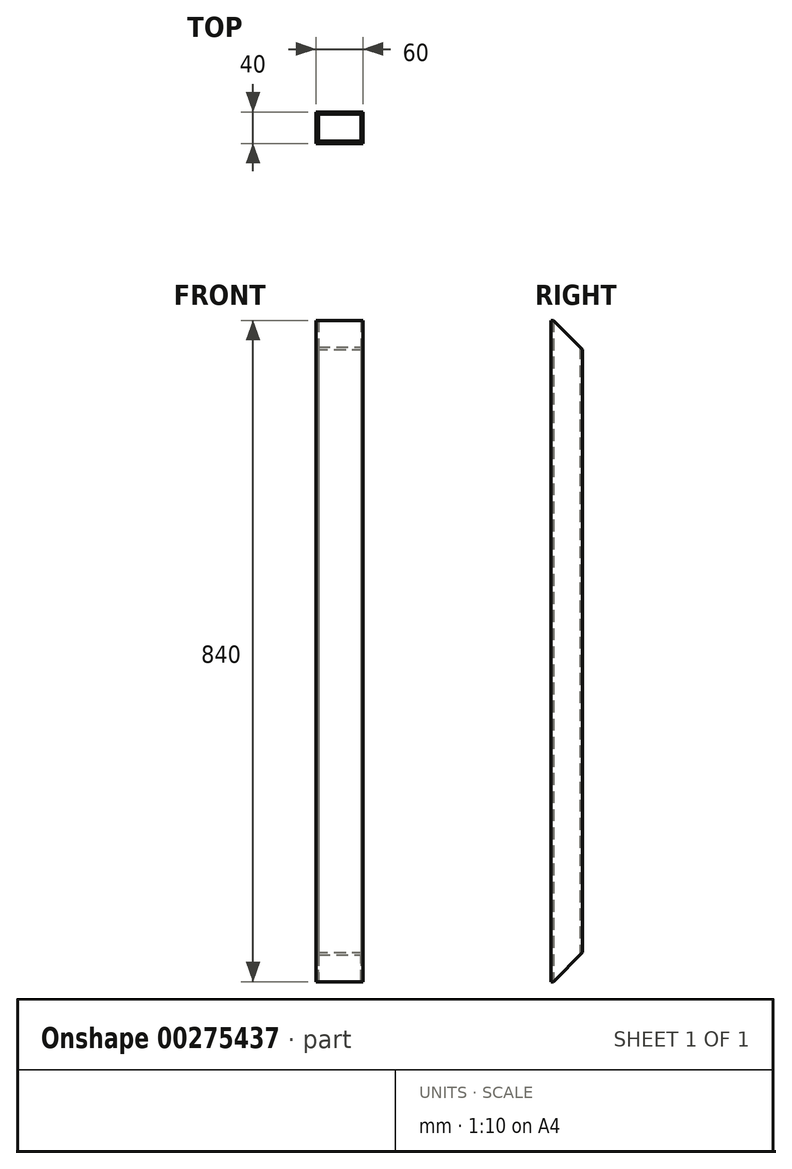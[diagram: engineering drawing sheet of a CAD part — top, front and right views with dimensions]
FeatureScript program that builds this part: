
annotation { "Feature Type Name" : "Feature", "Feature Type Description" : "" }
export const myFeature = defineFeature(function(context is Context, id is Id, definition is map)
    precondition{}
    {
        {
            var Q0;
            Q0=qCreatedBy(makeId("Top.planeOp"),FACE);
            var sketch = newSketch(context, id + "F0", { "sketchPlane" : qUnion([Q0])});
            skLineSegment(sketch, "E0.bottom", {"start": v(30, 20) * mm, "end": v(-30, 20) * mm});
            skLineSegment(sketch, "E0.top", {"start": v(30, -20) * mm, "end": v(-30, -20) * mm});
            skLineSegment(sketch, "E0.left", {"start": v(30, 20) * mm, "end": v(30, -20) * mm});
            skLineSegment(sketch, "E0.right", {"start": v(-30, 20) * mm, "end": v(-30, -20) * mm});
            skPoint(sketch, "E0.middle", {"position": v(0, 0) * mm});
            skLineSegment(sketch, "E1.bottom", {"start": v(27, 17) * mm, "end": v(-27, 17) * mm});
            skLineSegment(sketch, "E1.top", {"start": v(27, -17) * mm, "end": v(-27, -17) * mm});
            skLineSegment(sketch, "E1.left", {"start": v(27, 17) * mm, "end": v(27, -17) * mm});
            skLineSegment(sketch, "E1.right", {"start": v(-27, 17) * mm, "end": v(-27, -17) * mm});
            skSolve(sketch);
        }
        {
            var Q0;
            Q0=makeQuery(id+"F0.imprint","IMPRINT",FACE,{"disambiguationData":[TD([[makeQuery(id+"F0.imprint","IMPRINT",EDGE,{"derivedFrom":sQuery(id+"F0.wireOp",EDGE,"E0.bottom")}),1.0]])]});
            extrude(context, id + "F1", {"entities" : qUnion([Q0]), "depth" : 840 * mm});
        }
        {
            var Q0;
            Q0=makeQuery(id+"F1.opExtrude","SWEPT_FACE",FACE,{"disambiguationData":[OSD([sQuery(id+"F0.wireOp",EDGE,"E0.left")])]});
            var sketch = newSketch(context, id + "F2", { "sketchPlane" : qUnion([Q0])});
            skPoint(sketch, "E2", {"position": v(20, 803) * mm});
            skPoint(sketch, "E3", {"position": v(-17, 840) * mm});
            skLineSegment(sketch, "E4", {"start": v(-17, 840) * mm, "end": v(20, 803) * mm});
            skLineSegment(sketch, "E5", {"start": v(20, 840) * mm, "end": v(20, 803) * mm});
            skLineSegment(sketch, "E6", {"start": v(20, 840) * mm, "end": v(-17, 840) * mm});
            skPoint(sketch, "E7", {"position": v(-17, 0) * mm});
            skLineSegment(sketch, "E8", {"start": v(20, 0) * mm, "end": v(-17, 0) * mm});
            skPoint(sketch, "E9", {"position": v(20, 37) * mm});
            skLineSegment(sketch, "E10", {"start": v(-17, 0) * mm, "end": v(20, 37) * mm});
            skLineSegment(sketch, "E11", {"start": v(20, 0) * mm, "end": v(20, 37) * mm});
            skSolve(sketch);
        }
        {
            var Q0;
            Q0=qSketchRegion(id+"F2",true);
            var Q1;
            Q1=makeQuery(id+"F2.imprint","IMPRINT",FACE,{"disambiguationData":[TD([[makeQuery(id+"F2.imprint","IMPRINT",EDGE,{"derivedFrom":sQuery(id+"F2.wireOp",EDGE,"E4")}),1.0]])]});
            extrude(context, id + "F3", {"entities" : qUnion([Q0, Q1]), "operationType" : NewBodyOperationType.REMOVE, "oppositeDirection" : true, "depth" : 60 * mm});
        }
        {
            var Q0;
            Q0=makeQuery(id+"F2.imprint","IMPRINT",FACE,{"disambiguationData":[TD([[makeQuery(id+"F2.imprint","IMPRINT",EDGE,{"derivedFrom":sQuery(id+"F2.wireOp",EDGE,"E8")}),-1.0]])]});
            extrude(context, id + "F4", {"entities" : qUnion([Q0]), "operationType" : NewBodyOperationType.REMOVE, "oppositeDirection" : true, "depth" : 60 * mm});
        }
    });
